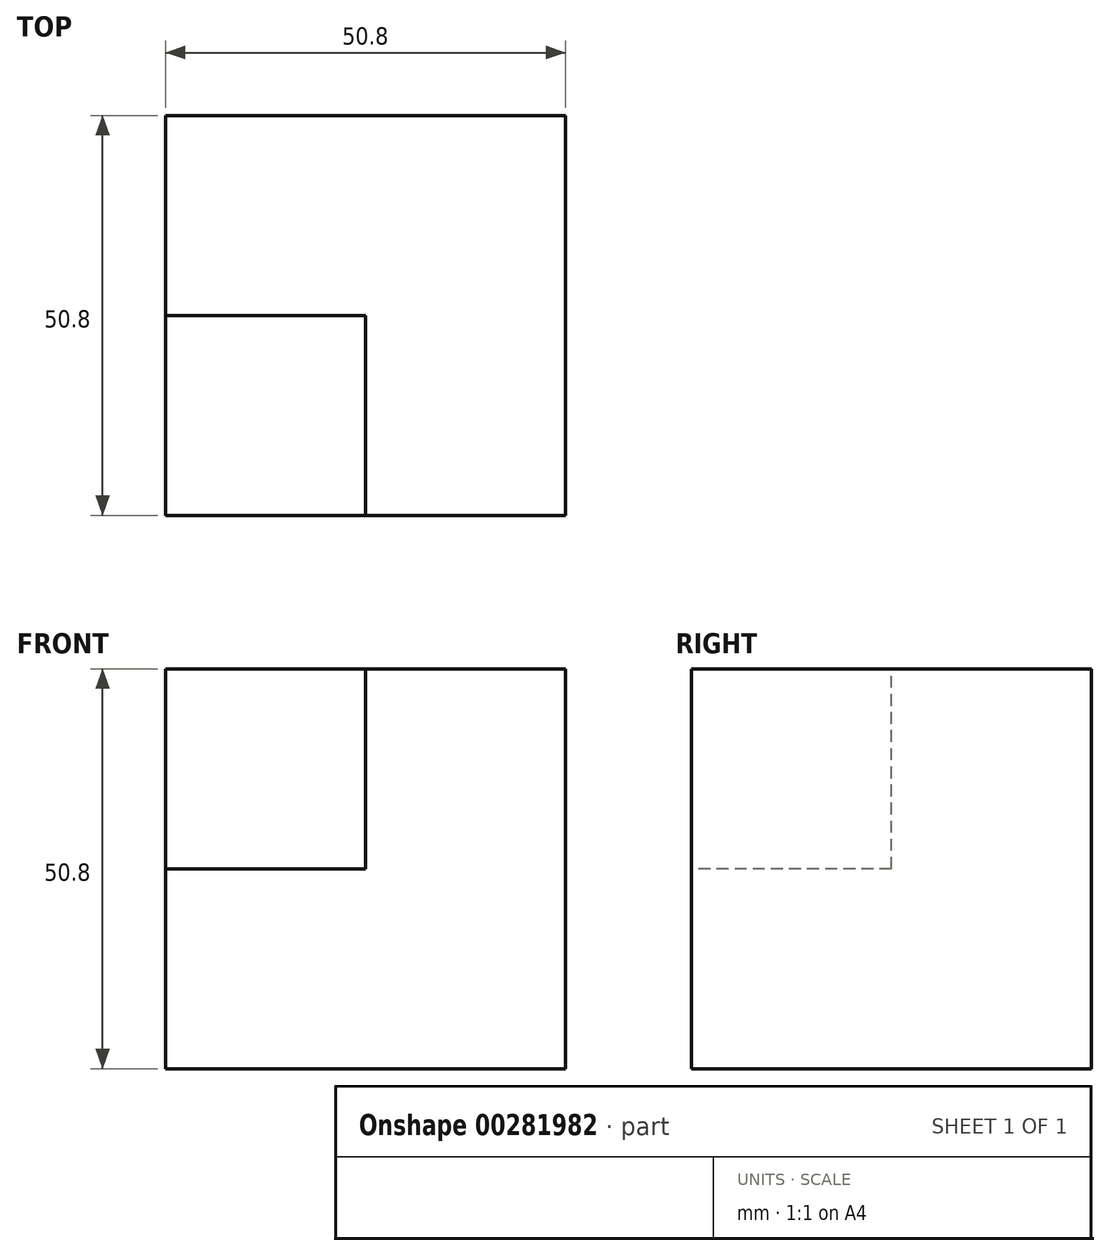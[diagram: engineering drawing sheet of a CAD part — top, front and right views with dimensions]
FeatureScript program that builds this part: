
annotation { "Feature Type Name" : "Feature", "Feature Type Description" : "" }
export const myFeature = defineFeature(function(context is Context, id is Id, definition is map)
    precondition{}
    {
        {
            var Q0;
            Q0=qCreatedBy(makeId("Front.planeOp"),FACE);
            var sketch = newSketch(context, id + "F0", { "sketchPlane" : qUnion([Q0])});
            skLineSegment(sketch, "E0", {"start": v(0, 0) * mm, "end": v(-50.8, 0) * mm});
            skLineSegment(sketch, "E1", {"start": v(-50.8, 0) * mm, "end": v(-50.8, 50.8) * mm});
            skLineSegment(sketch, "E2", {"start": v(0, 50.8) * mm, "end": v(0, 0) * mm});
            skLineSegment(sketch, "E3", {"start": v(0, 50.8) * mm, "end": v(-50.8, 50.8) * mm});
            skSolve(sketch);
        }
        {
            var Q0;
            Q0 = qSketchRegion(id + "F0", true);
            extrude(context, id + "F1", {"entities" : qUnion([Q0]), "depth" : 50.8 * mm});
        }
        {
            var Q0;
            Q0=makeQuery(id+"F1.opExtrude","CAP_FACE",FACE,{"disambiguationData":[OSD([sQuery(id+"F0.wireOp",EDGE,"E0"),sQuery(id+"F0.wireOp",EDGE,"E1"),sQuery(id+"F0.wireOp",EDGE,"E2"),sQuery(id+"F0.wireOp",EDGE,"E3")])],"isStart":false});
            var sketch = newSketch(context, id + "F2", { "sketchPlane" : qUnion([Q0])});
            skLineSegment(sketch, "E4.bottom", {"start": v(-50.8, 50.8) * mm, "end": v(-25.4, 50.8) * mm});
            skLineSegment(sketch, "E4.top", {"start": v(-50.8, 25.4) * mm, "end": v(-25.4, 25.4) * mm});
            skLineSegment(sketch, "E4.left", {"start": v(-50.8, 50.8) * mm, "end": v(-50.8, 25.4) * mm});
            skLineSegment(sketch, "E4.right", {"start": v(-25.4, 50.8) * mm, "end": v(-25.4, 25.4) * mm});
            skSolve(sketch);
        }
        {
            var Q0;
            Q0=makeQuery(id+"F2.imprint","IMPRINT",FACE,{"disambiguationData":[TD([[makeQuery(id+"F2.imprint","IMPRINT",EDGE,{"derivedFrom":sQuery(id+"F2.wireOp",EDGE,"E4.bottom")}),1.0]])]});
            extrude(context, id + "F3", {"entities" : qUnion([Q0]), "operationType" : NewBodyOperationType.REMOVE, "oppositeDirection" : true, "depth" : 25.4 * mm});
        }
    });
